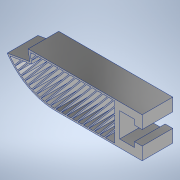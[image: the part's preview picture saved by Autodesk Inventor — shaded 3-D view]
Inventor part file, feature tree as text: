
AUTODESK INVENTOR PART (.ipt)
format: ipt  version: 2022 (Build 260153000, 153)  size: 425,984 bytes
history: native  units: mm
features: extrude x7, sketch x6, fillet x1, shell x1, projected_geometry x1
ambient origin geometry x8: Origin, YZ Plane, XZ Plane, XY Plane, X Axis, Y Axis, Z Axis, Center Point
bodies: Body1 (feature_tree)
feature tree (16):
  extrude  "Extrusion2"  Depth=5.8mm
  extrude  "Extrusion5"  Depth=12.0mm TaperAngle=0.0deg
  fillet  "Fillet2"  Radius=45.0mm
  shell  "Shell1"  Thickness=15.6mm
  extrude  "Extrusion7"  TaperAngle=0.0deg  [1 undecoded]
  extrude  "Extrusion8"  Depth=9.6mm
  extrude  "Extrusion9"  Depth=9.0mm
  extrude  "Extrusion10"  Depth=23.0mm
  extrude  "Extrusion11"  Depth=0.62mm
  sketch  "Sketch5"  dims[d41=5.8mm d48=44.0mm]
  sketch  "Sketch8"  dims[d50=3.0mm d56=12.0mm d57=0.0mm d63=45.0mm d67=15.6mm d71=0.0mm]
  sketch  "Sketch13"  dims[d80=17.453293mm d82=0.0mm d83=0.0mm]
  sketch  "Sketch14"  dims[d87=5.6mm d88=9.6mm]
  projected_geometry  "Projected Loop1"
  sketch  "Sketch16"  dims[d95=4.0mm d96=9.0mm]
  sketch  "Sketch17"  dims[d97=15.6mm d98=23.0mm d99=0.62mm d100=12.0mm d101=0.0mm d102=10.747401mm d103=12.0mm d104=0.0mm d105=0.38mm d1=0.38mm d127=12.0mm d128=0.0mm d130=22.68928mm d132=22.68928mm d133=0.38mm d135=0.38mm d136=0.38mm d137=0.38mm d138=0.38mm d139=0.38mm d140=0.38mm d141=0.38mm d143=0.38mm d152=22.68928mm d153=12.0mm d154=0.0mm d155=4.3mm d156=4.3mm d157=4.3mm d158=4.3mm d159=4.3mm d160=4.3mm d161=4.3mm d162=4.3mm d164=4.3mm d165=0.38mm d166=2.15mm d167=2.15mm d168=0.38mm d169=0.38mm d170=2.15mm d171=0.38mm d172=2.15mm d173=0.38mm d174=2.15mm d176=0.38mm d177=2.15mm d178=0.38mm d180=2.15mm d181=0.38mm d182=2.15mm d184=0.38mm d185=2.15mm d186=2.15mm d187=0.38mm d188=12.0mm d189=0.0mm d190=4.0mm]
note: 1 required parameter value undecoded (feature->parameter linkage not recoverable at this tier; creation-order binding heuristic only, values carry confidence <= 0.55)
